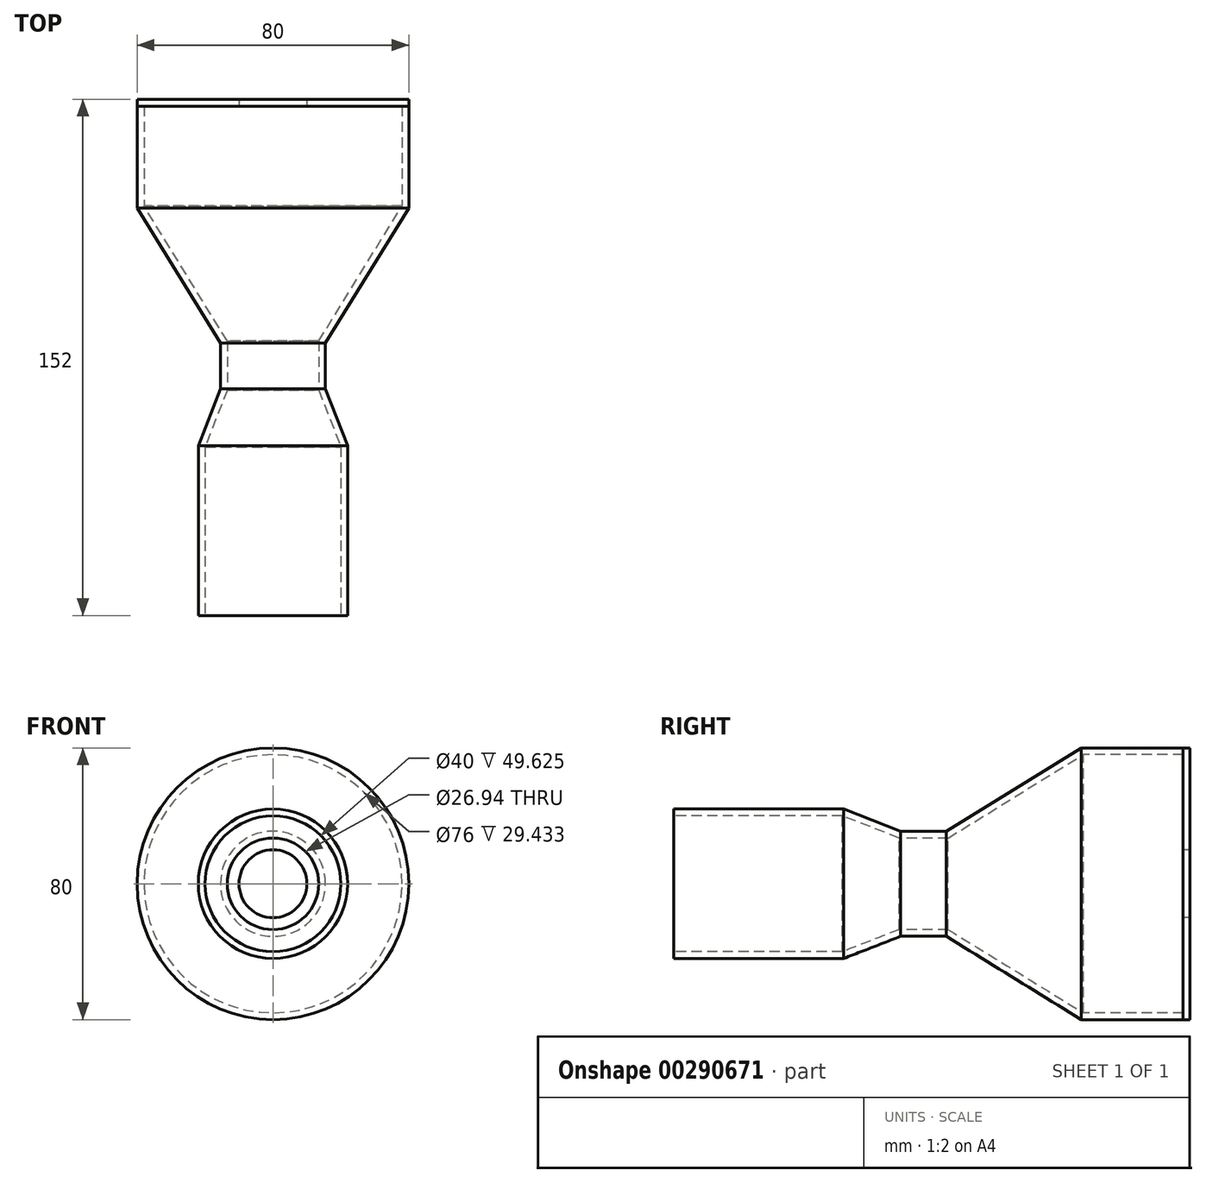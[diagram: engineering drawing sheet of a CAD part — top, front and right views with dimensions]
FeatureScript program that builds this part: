
annotation { "Feature Type Name" : "Feature", "Feature Type Description" : "" }
export const myFeature = defineFeature(function(context is Context, id is Id, definition is map)
    precondition{}
    {
        {
            var Q0;
            Q0=qCreatedBy(makeId("Right.planeOp"),FACE);
            var sketch = newSketch(context, id + "F0", { "sketchPlane" : qUnion([Q0])});
            skLineSegment(sketch, "E0", {"start": v(0, 22) * mm, "end": v(50, 22) * mm});
            skLineSegment(sketch, "E1", {"start": v(50, 22) * mm, "end": v(66.8, 15.47) * mm});
            skLineSegment(sketch, "E2", {"start": v(66.8, 15.47) * mm, "end": v(80.24, 15.47) * mm});
            skLineSegment(sketch, "E3", {"start": v(80.24, 15.47) * mm, "end": v(120, 40) * mm});
            skLineSegment(sketch, "E4", {"start": v(120, 40) * mm, "end": v(150, 40) * mm});
            skLineSegment(sketch, "E5.1", {"start": v(120.57, 38) * mm, "end": v(150, 38) * mm});
            skLineSegment(sketch, "E5.2", {"start": v(0, 20) * mm, "end": v(49.62, 20) * mm});
            skLineSegment(sketch, "E5.3", {"start": v(49.62, 20) * mm, "end": v(66.42, 13.47) * mm});
            skLineSegment(sketch, "E5.4", {"start": v(66.42, 13.47) * mm, "end": v(80.8, 13.47) * mm});
            skLineSegment(sketch, "E5.5", {"start": v(80.8, 13.47) * mm, "end": v(120.57, 38) * mm});
            skLineSegment(sketch, "E6", {"start": v(0, 22) * mm, "end": v(0, 20) * mm});
            skLineSegment(sketch, "E7", {"start": v(0, 0) * mm, "end": v(188.37, 0) * mm, "construction": true});
            skLineSegment(sketch, "E8", {"start": v(150, 38) * mm, "end": v(150, 40) * mm});
            skSolve(sketch);
        }
        {
            var Q0;
            Q0=makeQuery(id+"F0.imprint","IMPRINT",FACE,{"disambiguationData":[TD([[makeQuery(id+"F0.imprint","IMPRINT",EDGE,{"derivedFrom":sQuery(id+"F0.wireOp",EDGE,"E0")}),-1.0]])]});
            var Q1;
            Q1=sQuery(id+"F0.wireOp",EDGE,"E7");
            revolve(context, id + "F1", {"entities" : qUnion([Q0]), "axis" : qUnion([Q1]), "revolveType" : RevolveType.FULL});
        }
        {
            var Q0;
            Q0=qCreatedBy(makeId("Right.planeOp"),FACE);
            var sketch = newSketch(context, id + "F2", { "sketchPlane" : qUnion([Q0])});
            skLineSegment(sketch, "E9.0", {"start": v(150, -40) * mm, "end": v(150, 40) * mm, "construction": true});
            skLineSegment(sketch, "E10.bottom", {"start": v(150, 40) * mm, "end": v(152, 40) * mm});
            skLineSegment(sketch, "E10.top", {"start": v(150, 10) * mm, "end": v(152, 10) * mm});
            skLineSegment(sketch, "E10.left", {"start": v(150, 40) * mm, "end": v(150, 10) * mm});
            skLineSegment(sketch, "E10.right", {"start": v(152, 40) * mm, "end": v(152, 10) * mm});
            skLineSegment(sketch, "E11", {"start": v(0, 0) * mm, "end": v(183.17, 0) * mm, "construction": true});
            skSolve(sketch);
        }
        {
            var Q0;
            Q0 = qSketchRegion(id + "F2", true);
            var Q1;
            Q1=sQuery(id+"F2.wireOp",EDGE,"E11");
            revolve(context, id + "F3", {"entities" : qUnion([Q0]), "axis" : qUnion([Q1]), "revolveType" : RevolveType.FULL});
        }
    });
